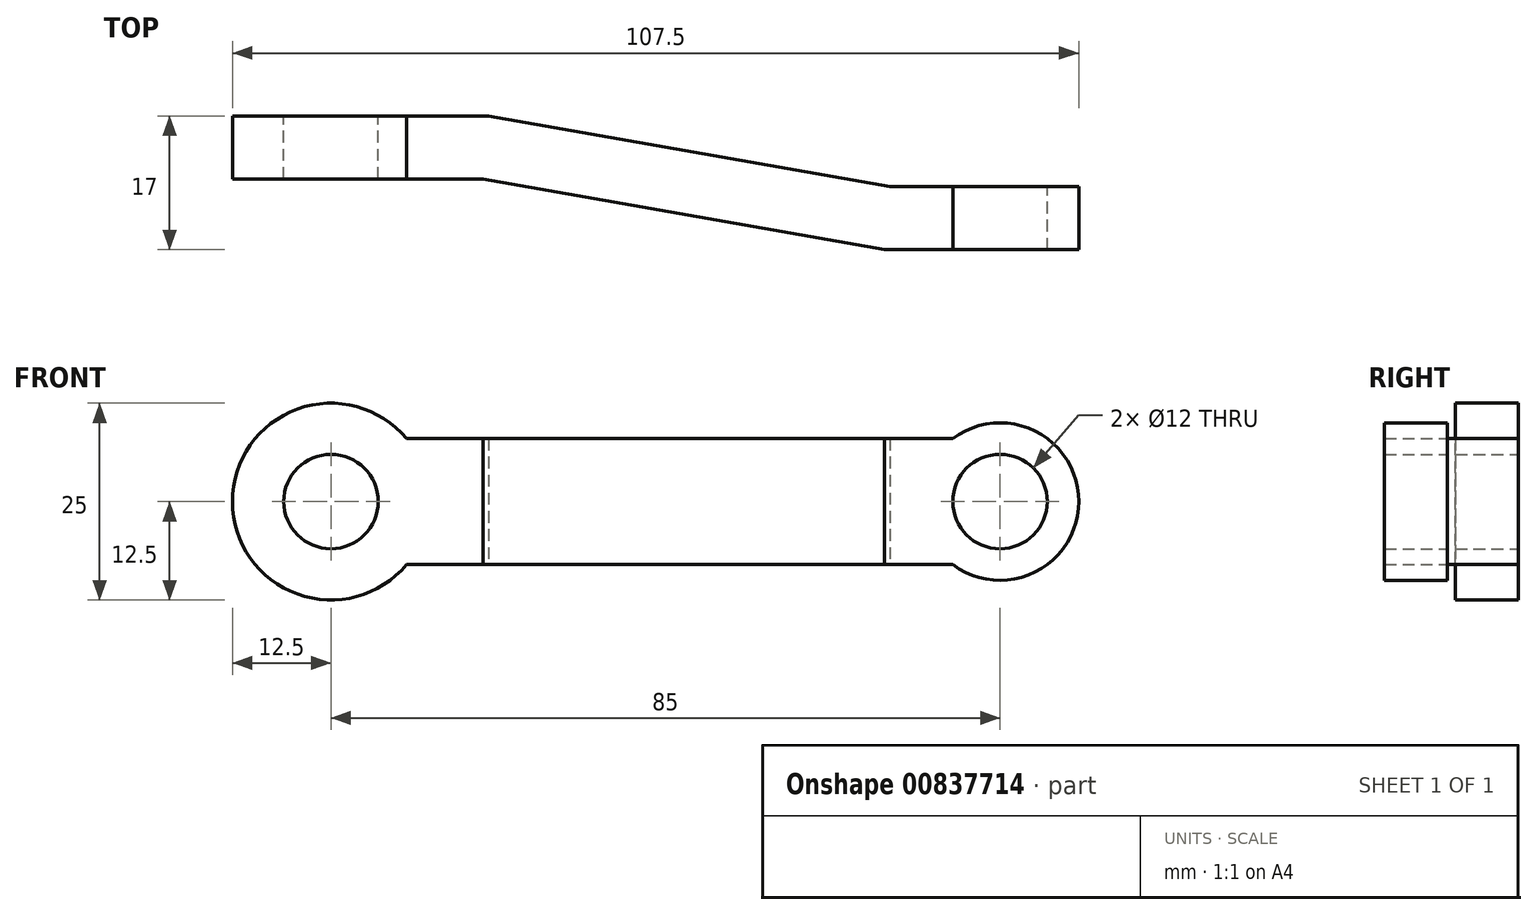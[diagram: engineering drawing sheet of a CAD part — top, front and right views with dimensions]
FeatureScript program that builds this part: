
annotation { "Feature Type Name" : "Feature", "Feature Type Description" : "" }
export const myFeature = defineFeature(function(context is Context, id is Id, definition is map)
    precondition{}
    {
        {
            var Q0;
            Q0=qCreatedBy(makeId("Front.planeOp"),FACE);
            var sketch = newSketch(context, id + "F0", { "sketchPlane" : qUnion([Q0])});
            skCircle(sketch, "E0", {"center": v(0, 0) * mm, "radius": 12.5 * mm});
            skCircle(sketch, "E1", {"center": v(85, 0) * mm, "radius": 10 * mm});
            skLineSegment(sketch, "E2", {"start": v(0, 0) * mm, "end": v(85, 0) * mm, "construction": true});
            skLineSegment(sketch, "E3", {"start": v(9.6, 8) * mm, "end": v(79, 8) * mm});
            skLineSegment(sketch, "E4.MirrorCS", {"start": v(9.6, -8) * mm, "end": v(79, -8) * mm});
            skCircle(sketch, "E5", {"center": v(0, 0) * mm, "radius": 6 * mm});
            skCircle(sketch, "E6", {"center": v(85, 0) * mm, "radius": 6 * mm});
            skSolve(sketch);
        }
        {
            var Q0;
            Q0=makeQuery(id+"F0.imprint","IMPRINT",FACE,{"disambiguationData":[TD([[makeQuery(id+"F0.imprint","IMPRINT",EDGE,{"derivedFrom":sQuery(id+"F0.wireOp",EDGE,"E5")}),-1.0]])]});
            var Q1;
            Q1=makeQuery(id+"F0.imprint","IMPRINT",FACE,{"disambiguationData":[TD([[makeQuery(id+"F0.imprint","IMPRINT",EDGE,{"derivedFrom":sQuery(id+"F0.wireOp",EDGE,"E6")}),-1.0]])]});
            var Q2;
            {var subQ0=sQuery(id+"F0.wireOp",EDGE,"E3");Q2=makeQuery(id+"F0.imprint","IMPRINT",FACE,{"disambiguationData":[TD([[makeQuery(id+"F0.imprint","IMPRINT",EDGE,{"derivedFrom":subQ0}),-1.0]])]});}
            extrude(context, id + "F1", {"entities" : qUnion([Q0, Q1, Q2]), "depth" : 25 * mm, "offsetDistance" : 25 * mm});
        }
        {
            var Q0;
            Q0=qCreatedBy(makeId("Top.planeOp"),FACE);
            var sketch = newSketch(context, id + "F2", { "sketchPlane" : qUnion([Q0])});
            skLineSegment(sketch, "E7", {"start": v(-12.5, 0) * mm, "end": v(20, 0) * mm});
            skLineSegment(sketch, "E8", {"start": v(20, 0) * mm, "end": v(71.04, -9) * mm});
            skLineSegment(sketch, "E9", {"start": v(71.04, -9) * mm, "end": v(95, -9) * mm});
            skLineSegment(sketch, "E10.0", {"start": v(70.34, -17) * mm, "end": v(95, -17) * mm});
            skLineSegment(sketch, "E10.1", {"start": v(19.3, -8) * mm, "end": v(70.34, -17) * mm});
            skLineSegment(sketch, "E10.2", {"start": v(-12.5, -8) * mm, "end": v(19.3, -8) * mm});
            skLineSegment(sketch, "E11", {"start": v(-12.5, -8) * mm, "end": v(-12.5, 0) * mm});
            skLineSegment(sketch, "E12", {"start": v(95, -17) * mm, "end": v(95, -9) * mm});
            skLineSegment(sketch, "E13", {"start": v(-12.5, -25) * mm, "end": v(-12.5, 0) * mm});
            skLineSegment(sketch, "E14", {"start": v(95, 0) * mm, "end": v(95, -25) * mm});
            skSolve(sketch);
        }
        {
            var Q0;
            Q0=makeQuery(id+"F2.imprint","IMPRINT",FACE,{"disambiguationData":[TD([[makeQuery(id+"F2.imprint","IMPRINT",EDGE,{"derivedFrom":sQuery(id+"F2.wireOp",EDGE,"E7")}),-1.0]])]});
            extrude(context, id + "F3", {"entities" : qUnion([Q0]), "operationType" : NewBodyOperationType.INTERSECT, "endBound" : BoundingType.SYMMETRIC, "depth" : 25 * mm, "offsetDistance" : 25 * mm});
        }
    });
